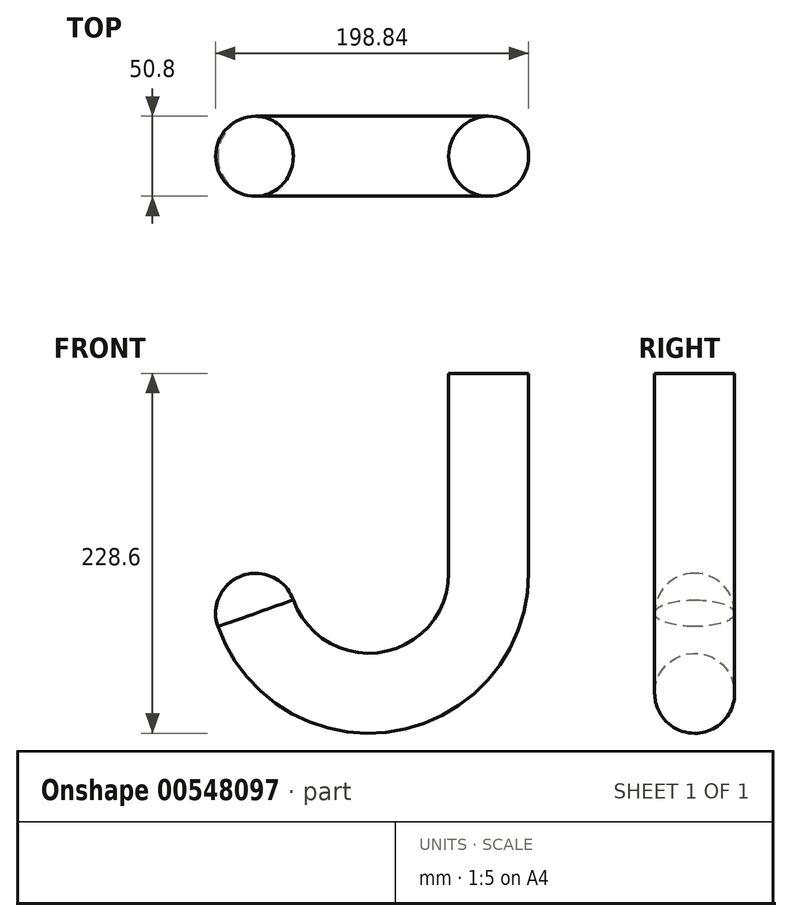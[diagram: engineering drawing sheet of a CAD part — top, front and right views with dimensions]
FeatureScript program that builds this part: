
annotation { "Feature Type Name" : "Feature", "Feature Type Description" : "" }
export const myFeature = defineFeature(function(context is Context, id is Id, definition is map)
    precondition{}
    {
        {
            var Q0;
            Q0=qCreatedBy(makeId("Front.planeOp"),FACE);
            var sketch = newSketch(context, id + "F0", { "sketchPlane" : qUnion([Q0])});
            skLineSegment(sketch, "E0", {"start": v(0, 0) * mm, "end": v(0, -127) * mm});
            skArc(sketch, "E1", {"start": v(-152.4, -127) * mm, "mid": v(-76.2, -203.2) * mm, "end": v(0, -127) * mm});
            skSolve(sketch);
        }
        {
            var Q0;
            Q0=qCreatedBy(makeId("Top.planeOp"),FACE);
            var sketch = newSketch(context, id + "F1", { "sketchPlane" : qUnion([Q0])});
            skCircle(sketch, "E2", {"center": v(0, 0) * mm, "radius": 25.4 * mm});
            skSolve(sketch);
        }
        {
            var Q0;
            Q0=makeQuery(id+"F1.imprint","IMPRINT",FACE,{"disambiguationData":[TD([[makeQuery(id+"F1.imprint","IMPRINT",EDGE,{"derivedFrom":sQuery(id+"F1.wireOp",EDGE,"E2")}),1.0]])]});
            var Q1;
            Q1=sQuery(id+"F0.wireOp",EDGE,"E0");
            var Q2;
            Q2=sQuery(id+"F0.wireOp",EDGE,"E1");
            sweep(context, id + "F2", {"profiles" : qUnion([Q0]), "path" : qUnion([Q1, Q2])});
        }
        {
            var Q0;
            Q0=makeQuery(id+"F2.opSweep","CAP_EDGE",EDGE,{"disambiguationData":[OSD([sQuery(id+"F0.wireOp",VERTEX,"E1.start"),sQuery(id+"F1.wireOp",EDGE,"E2")])],"isStart":false});
            fillet(context, id + "F3", {"entities" : qUnion([Q0]), "radius" : 25.4 * mm, "tangentPropagation" : true, "allowEdgeOverflow" : false});
        }
    });
